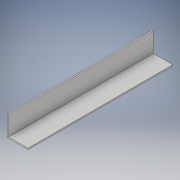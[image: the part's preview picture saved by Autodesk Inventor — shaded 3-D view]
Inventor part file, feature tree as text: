
AUTODESK INVENTOR PART (.ipt)
format: ipt  version: 2018 (Build 220112000, 112)  size: 94,720 bytes
history: native  units: in
note: dims shown in document units (in); Inventor stores cm internally (conversion verified against a paired STEP export)
features: extrude x1, sketch x1
ambient origin geometry x8: Origin, YZ Plane, XZ Plane, XY Plane, X Axis, Y Axis, Z Axis, Center Point
bodies: Body1 (feature_tree)
feature tree (2):
  extrude  "Extrusion2"  [1 undecoded]
  sketch  "Sketch1"  dims[d7=7.0in d8=0.0in]
note: 1 required parameter value undecoded (feature->parameter linkage not recoverable at this tier; creation-order binding heuristic only, values carry confidence <= 0.55)
